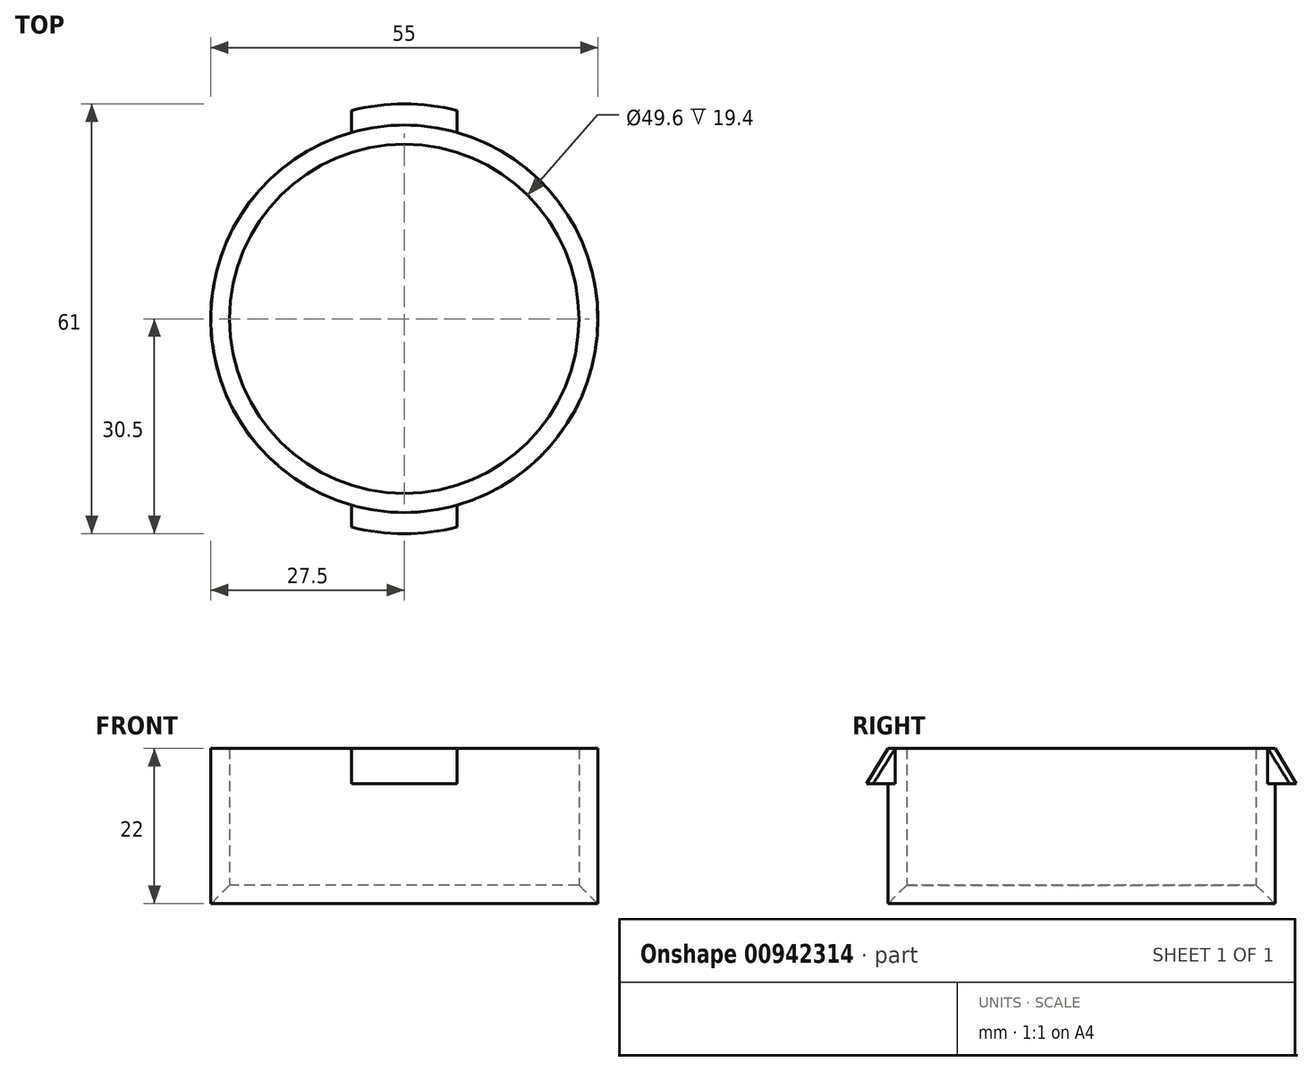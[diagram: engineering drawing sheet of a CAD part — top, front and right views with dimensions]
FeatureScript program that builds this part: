
annotation { "Feature Type Name" : "Feature", "Feature Type Description" : "" }
export const myFeature = defineFeature(function(context is Context, id is Id, definition is map)
    precondition{}
    {
        {
            var Q0;
            Q0=qCreatedBy(makeId("Top.planeOp"),FACE);
            var sketch = newSketch(context, id + "F0", { "sketchPlane" : qUnion([Q0])});
            skCircle(sketch, "E0", {"center": v(0, 0) * mm, "radius": 27.5 * mm});
            skCircle(sketch, "E1", {"center": v(0, 0) * mm, "radius": 24.8 * mm});
            skSolve(sketch);
        }
        {
            var Q0;
            Q0=makeQuery(id+"F0.imprint","IMPRINT",FACE,{"disambiguationData":[TD([[makeQuery(id+"F0.imprint","IMPRINT",EDGE,{"derivedFrom":sQuery(id+"F0.wireOp",EDGE,"E0")}),1.0]])]});
            extrude(context, id + "F1", {"entities" : qUnion([Q0]), "depth" : 22 * mm, "offsetDistance" : 25 * mm});
        }
        {
            var Q0;
            Q0=qCreatedBy(makeId("Right.planeOp"),FACE);
            var sketch = newSketch(context, id + "F2", { "sketchPlane" : qUnion([Q0])});
            skLineSegment(sketch, "E2.0", {"start": v(-27.5, 22) * mm, "end": v(27.5, 22) * mm});
            skLineSegment(sketch, "E3", {"start": v(-27.5, 0) * mm, "end": v(-27.5, 22) * mm});
            skLineSegment(sketch, "E4", {"start": v(-27.5, 22) * mm, "end": v(-30.5, 17) * mm});
            skLineSegment(sketch, "E5", {"start": v(-30.5, 17) * mm, "end": v(-27.5, 17) * mm});
            skLineSegment(sketch, "E6", {"start": v(-27.5, 17) * mm, "end": v(-27.5, 22) * mm});
            skSolve(sketch);
        }
        {
            var Q0;
            {var subQ0=sQuery(id+"F2.wireOp",EDGE,"E4");Q0=makeQuery(id+"F2.imprint","IMPRINT",FACE,{"disambiguationData":[TD([[makeQuery(id+"F2.imprint","IMPRINT",EDGE,{"derivedFrom":subQ0}),1.0]])]});}
            var Q1;
            Q1=makeQuery(id+"F1.opExtrude","SWEPT_FACE",FACE,{"disambiguationData":[OSD([sQuery(id+"F0.wireOp",EDGE,"E1")])]});
            revolve(context, id + "F3", {"operationType" : NewBodyOperationType.ADD, "surfaceOperationType" : NewSurfaceOperationType.NEW, "entities" : qUnion([Q0]), "axis" : qUnion([Q1]), "revolveType" : RevolveType.FULL});
        }
        {
            var Q0;
            Q0=qCreatedBy(makeId("Top.planeOp"),FACE);
            var sketch = newSketch(context, id + "F4", { "sketchPlane" : qUnion([Q0])});
            skLineSegment(sketch, "E7.bottom", {"start": v(-7.5, 35.98) * mm, "end": v(7.5, 35.98) * mm});
            skLineSegment(sketch, "E7.top", {"start": v(-7.5, -34.02) * mm, "end": v(7.5, -34.02) * mm});
            skLineSegment(sketch, "E7.left", {"start": v(-7.5, 35.98) * mm, "end": v(-7.5, 26.46) * mm});
            skLineSegment(sketch, "E7.right", {"start": v(7.5, 35.98) * mm, "end": v(7.5, 26.46) * mm});
            skLineSegment(sketch, "E8.bottom", {"start": v(-41.06, 46.32) * mm, "end": v(39.13, 46.32) * mm});
            skLineSegment(sketch, "E8.top", {"start": v(-41.06, -45) * mm, "end": v(39.13, -45) * mm});
            skLineSegment(sketch, "E8.left", {"start": v(-41.06, 46.32) * mm, "end": v(-41.06, -45) * mm});
            skLineSegment(sketch, "E8.right", {"start": v(39.13, 46.32) * mm, "end": v(39.13, -45) * mm});
            skCircle(sketch, "E9", {"center": v(0, 0) * mm, "radius": 27.5 * mm});
            skLineSegment(sketch, "E10.trimOffspring", {"start": v(7.5, -26.46) * mm, "end": v(7.5, -34.02) * mm});
            skLineSegment(sketch, "E11.trimOffspring", {"start": v(-7.5, -26.46) * mm, "end": v(-7.5, -34.02) * mm});
            skSolve(sketch);
        }
        {
            var Q0;
            Q0=makeQuery(id+"F4.imprint","IMPRINT",FACE,{"disambiguationData":[TD([[makeQuery(id+"F4.imprint","IMPRINT",EDGE,{"derivedFrom":sQuery(id+"F4.wireOp",EDGE,"E7.bottom")}),1.0]])]});
            extrude(context, id + "F5", {"entities" : qUnion([Q0]), "operationType" : NewBodyOperationType.REMOVE, "depth" : 42.3 * mm, "offsetDistance" : 25 * mm});
        }
        {
            var Q0;
            Q0=makeQuery(id+"F1.opExtrude","CAP_EDGE",EDGE,{"disambiguationData":[OSD([sQuery(id+"F0.wireOp",EDGE,"E1")])],"isStart":true});
            chamfer(context, id + "F6", {"entities" : qUnion([Q0]), "width" : 2.6 * mm, "tangentPropagation" : true});
        }
    });
